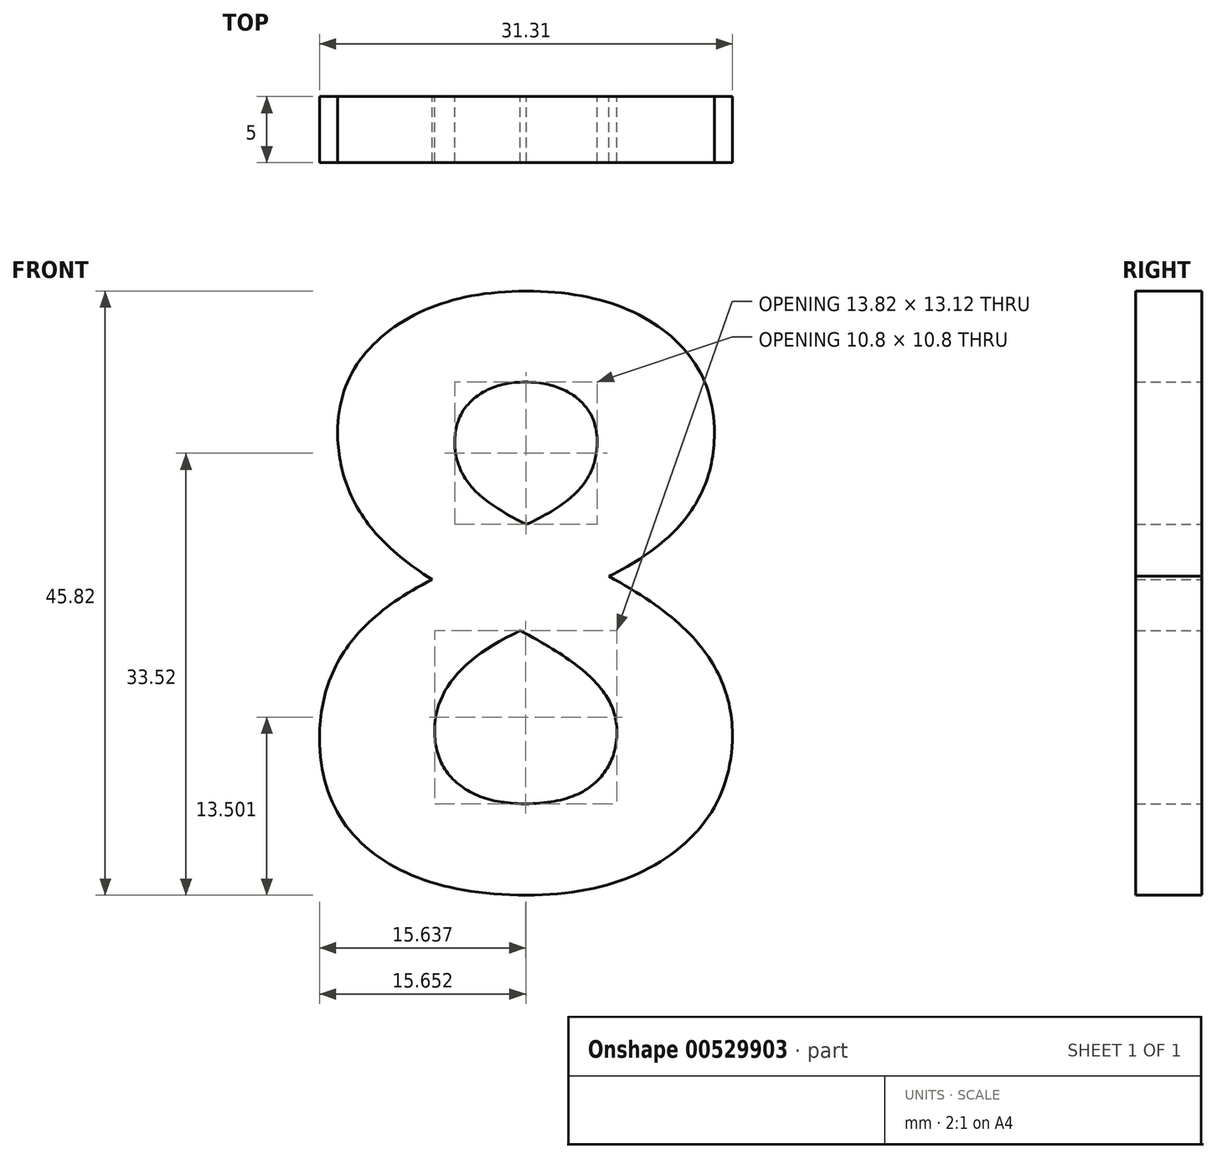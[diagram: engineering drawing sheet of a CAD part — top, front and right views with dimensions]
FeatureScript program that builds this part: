
annotation { "Feature Type Name" : "Feature", "Feature Type Description" : "" }
export const myFeature = defineFeature(function(context is Context, id is Id, definition is map)
    precondition{}
    {
        {
            var Q0;
            Q0=qCreatedBy(makeId("Front.planeOp"),FACE);
            var sketch = newSketch(context, id + "F0", { "sketchPlane" : qUnion([Q0])});
            skText(sketch, "E0", { "text": "8", "fontName": "OpenSans-Bold.ttf"});
            const initialGuessF0  = {"E0": [-0.05975, 0.01496, 1, 0, 0.045]};
            skSetInitialGuess(sketch, initialGuessF0);
            skSolve(sketch);
        }
        {
            var Q0;
            Q0=makeQuery(id+"F0.imprint","IMPRINT",FACE,{"disambiguationData":[TD([[makeQuery(id+"F0.imprint","IMPRINT",EDGE,{"derivedFrom":sQuery(id+"F0.wireOp",EDGE,"E0.sketch_text.stroke-0")}),-1.0]])]});
            extrude(context, id + "F1", {"entities" : qUnion([Q0]), "depth" : 5 * mm, "offsetDistance" : 25 * mm});
        }
    });
